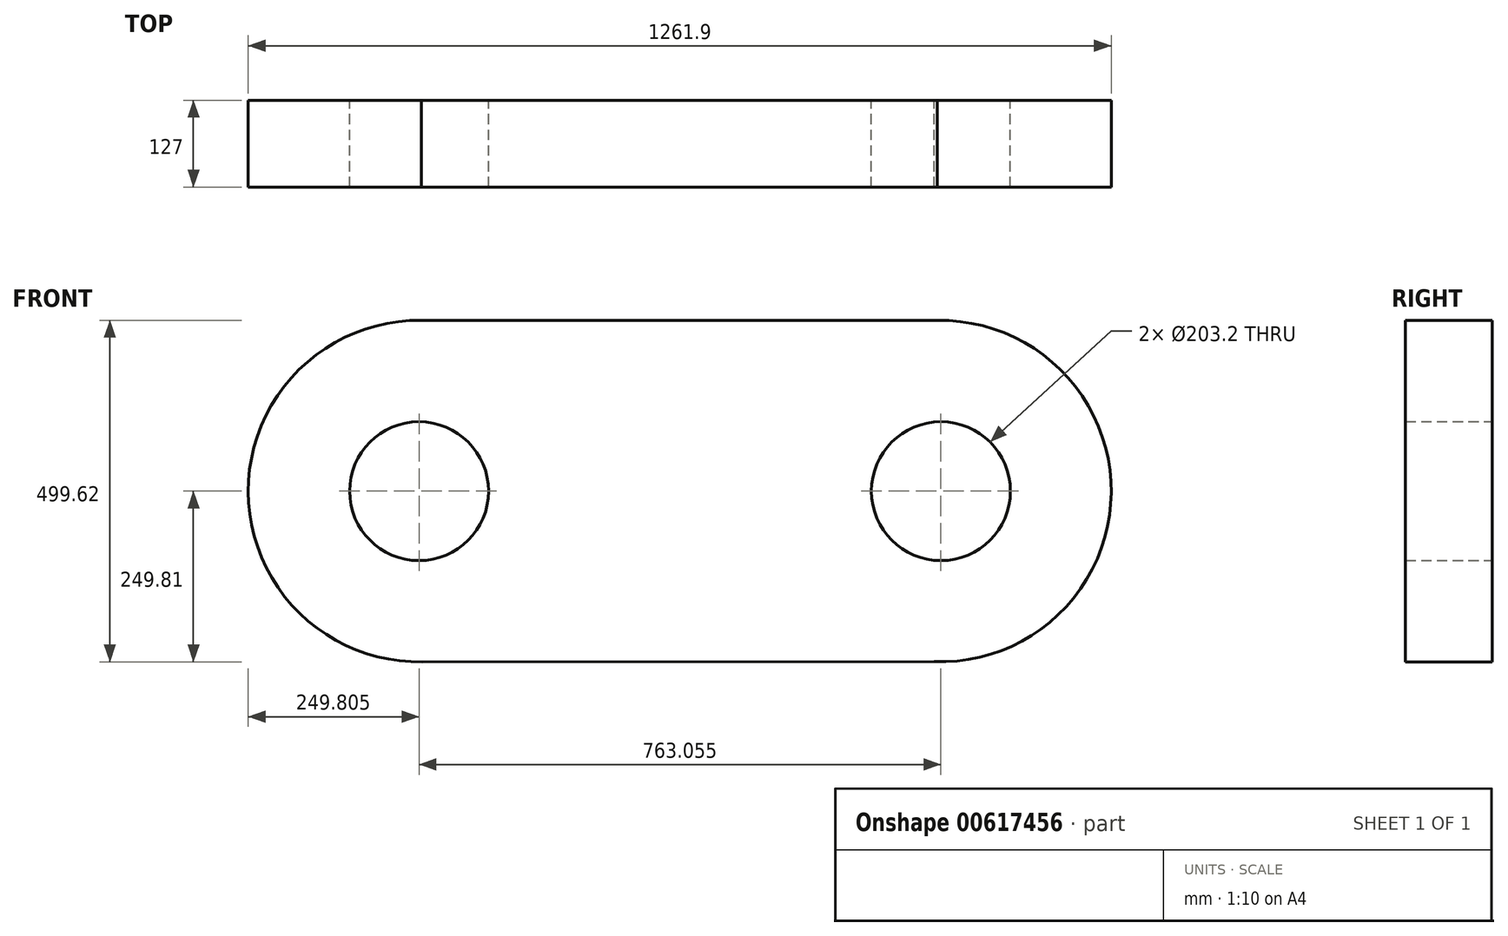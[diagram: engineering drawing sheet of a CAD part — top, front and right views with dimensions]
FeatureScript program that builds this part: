
annotation { "Feature Type Name" : "Feature", "Feature Type Description" : "" }
export const myFeature = defineFeature(function(context is Context, id is Id, definition is map)
    precondition{}
    {
        {
            var Q0;
            Q0=qCreatedBy(makeId("Front.planeOp"),FACE);
            var sketch = newSketch(context, id + "F0", { "sketchPlane" : qUnion([Q0])});
            skLineSegment(sketch, "E0", {"start": v(-355.47, 0) * mm, "end": v(406.53, 0) * mm});
            skCircle(sketch, "E1", {"center": v(-355.45, 0) * mm, "radius": 249.8 * mm});
            skCircle(sketch, "E2", {"center": v(406.85, 0) * mm, "radius": 249.8 * mm});
            skCircle(sketch, "E3", {"center": v(-355.45, 0) * mm, "radius": 101.6 * mm});
            skCircle(sketch, "E4", {"center": v(407.6, 0) * mm, "radius": 101.6 * mm});
            skLineSegment(sketch, "E5", {"start": v(-352.23, 249.79) * mm, "end": v(402.37, 249.77) * mm});
            skLineSegment(sketch, "E6", {"start": v(415.84, -249.65) * mm, "end": v(-360.24, -249.76) * mm});
            skSolve(sketch);
        }
        {
            var Q0;
            Q0 = qSketchRegion(id + "F0", true);
            extrude(context, id + "F1", {"entities" : qUnion([Q0]), "depth" : 127 * mm, "offsetDistance" : 25.4 * mm});
        }
    });
